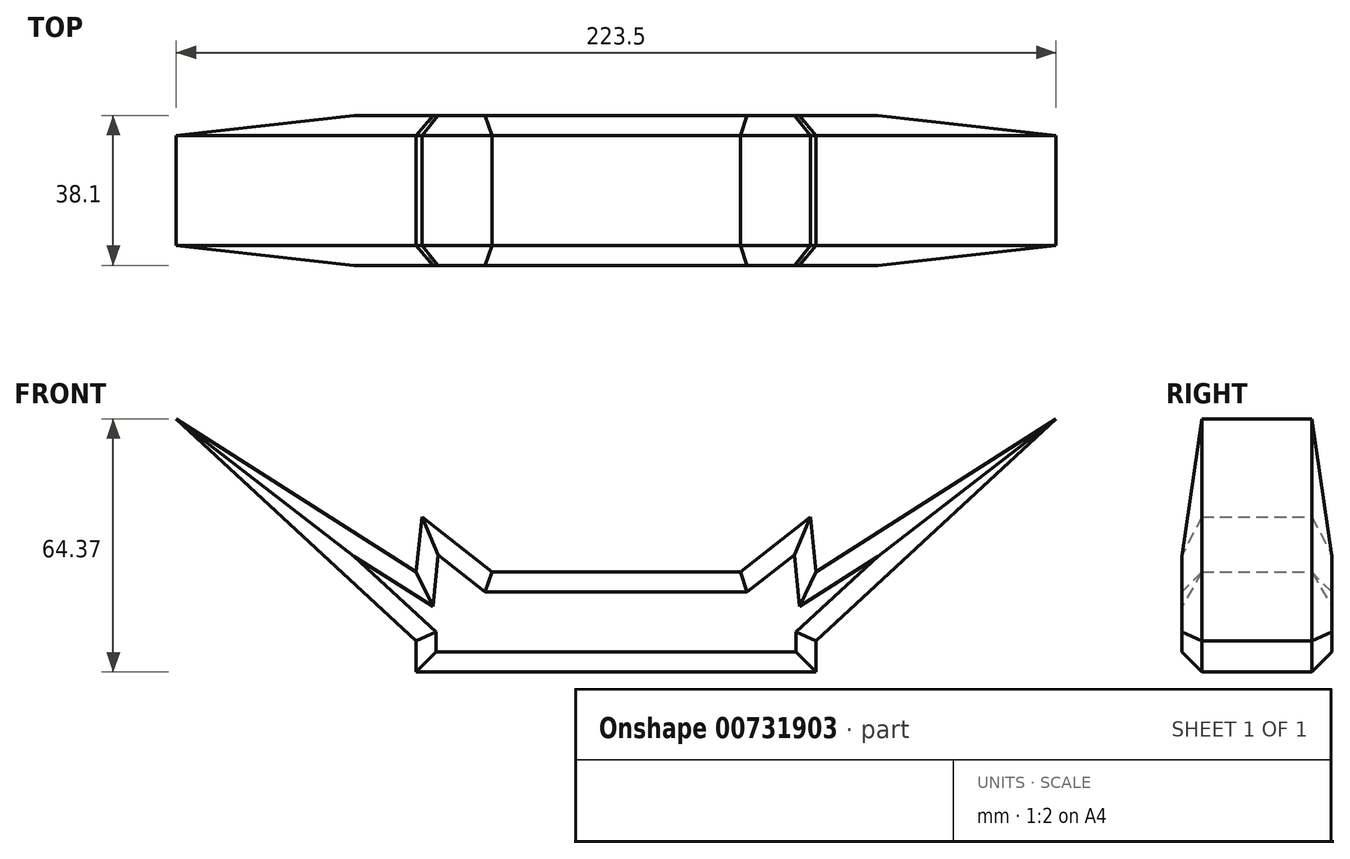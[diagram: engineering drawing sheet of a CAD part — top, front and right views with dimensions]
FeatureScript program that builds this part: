
annotation { "Feature Type Name" : "Feature", "Feature Type Description" : "" }
export const myFeature = defineFeature(function(context is Context, id is Id, definition is map)
    precondition{}
    {
        {
            var Q0;
            Q0=qCreatedBy(makeId("Front.planeOp"),FACE);
            var sketch = newSketch(context, id + "F0", { "sketchPlane" : qUnion([Q0])});
            skLineSegment(sketch, "E0", {"start": v(0, 12.7) * mm, "end": v(50.8, 12.7) * mm});
            skLineSegment(sketch, "E1", {"start": v(50.8, 12.7) * mm, "end": v(50.8, -12.7) * mm});
            skLineSegment(sketch, "E2", {"start": v(50.8, -12.7) * mm, "end": v(0, -12.7) * mm});
            skLineSegment(sketch, "E3.MirrorCS", {"start": v(0, 12.7) * mm, "end": v(-50.8, 12.7) * mm});
            skLineSegment(sketch, "E4.MirrorCS", {"start": v(-50.8, -12.7) * mm, "end": v(0, -12.7) * mm});
            skLineSegment(sketch, "E5.MirrorCS", {"start": v(-50.8, 12.7) * mm, "end": v(-50.8, -12.7) * mm});
            skLineSegment(sketch, "E6", {"start": v(-31.53, 12.7) * mm, "end": v(-49.37, 26.74) * mm});
            skLineSegment(sketch, "E7", {"start": v(-49.37, 26.74) * mm, "end": v(-50.8, 12.7) * mm});
            skLineSegment(sketch, "E8", {"start": v(-50.8, 12.7) * mm, "end": v(-111.75, 51.67) * mm});
            skLineSegment(sketch, "E9", {"start": v(-111.75, 51.67) * mm, "end": v(-50.8, -4.75) * mm});
            skLineSegment(sketch, "E10", {"start": v(0, 12.7) * mm, "end": v(0, -12.7) * mm});
            skLineSegment(sketch, "E11.MirrorCS", {"start": v(31.53, 12.7) * mm, "end": v(49.37, 26.74) * mm});
            skLineSegment(sketch, "E12.MirrorCS", {"start": v(49.37, 26.74) * mm, "end": v(50.8, 12.7) * mm});
            skLineSegment(sketch, "E13.MirrorCS", {"start": v(50.8, 12.7) * mm, "end": v(111.75, 51.67) * mm});
            skLineSegment(sketch, "E14.MirrorCS", {"start": v(111.75, 51.67) * mm, "end": v(50.8, -4.75) * mm});
            skSolve(sketch);
        }
        {
            var Q0;
            {var subQ0=sQuery(id+"F0.wireOp",EDGE,"E2");Q0=makeQuery(id+"F0.imprint","IMPRINT",FACE,{"disambiguationData":[TD([[makeQuery(id+"F0.imprint","IMPRINT",EDGE,{"derivedFrom":subQ0}),-1.0]])]});}
            var Q1;
            {var subQ2=sQuery(id+"F0.wireOp",EDGE,"E11.MirrorCS");Q1=makeQuery(id+"F0.imprint","IMPRINT",FACE,{"disambiguationData":[TD([[makeQuery(id+"F0.imprint","IMPRINT",EDGE,{"derivedFrom":subQ2}),-1.0]])]});}
            var Q2;
            {var subQ0=sQuery(id+"F0.wireOp",EDGE,"E13.MirrorCS");Q2=makeQuery(id+"F0.imprint","IMPRINT",FACE,{"disambiguationData":[TD([[makeQuery(id+"F0.imprint","IMPRINT",EDGE,{"derivedFrom":subQ0}),-1.0]])]});}
            var Q3;
            {var subQ2=sQuery(id+"F0.wireOp",EDGE,"E6");Q3=makeQuery(id+"F0.imprint","IMPRINT",FACE,{"disambiguationData":[TD([[makeQuery(id+"F0.imprint","IMPRINT",EDGE,{"derivedFrom":subQ2}),1.0]])]});}
            var Q4;
            {var subQ0=sQuery(id+"F0.wireOp",EDGE,"E8");Q4=makeQuery(id+"F0.imprint","IMPRINT",FACE,{"disambiguationData":[TD([[makeQuery(id+"F0.imprint","IMPRINT",EDGE,{"derivedFrom":subQ0}),1.0]])]});}
            var Q5;
            {var subQ4=sQuery(id+"F0.wireOp",EDGE,"E4.MirrorCS");Q5=makeQuery(id+"F0.imprint","IMPRINT",FACE,{"disambiguationData":[TD([[makeQuery(id+"F0.imprint","IMPRINT",EDGE,{"derivedFrom":subQ4}),1.0]])]});}
            extrude(context, id + "F1", {"entities" : qUnion([Q0, Q1, Q2, Q3, Q4, Q5]), "depth" : 19.05 * mm, "offsetDistance" : 25.4 * mm});
        }
        {
            var Q0;
            Q0=makeQuery(id+"F1.opExtrude","CAP_FACE",FACE,{"disambiguationData":[OSD([sQuery(id+"F0.wireOp",EDGE,"E0"),sQuery(id+"F0.wireOp",EDGE,"E1"),sQuery(id+"F0.wireOp",EDGE,"E2"),sQuery(id+"F0.wireOp",EDGE,"E3.MirrorCS"),sQuery(id+"F0.wireOp",EDGE,"E4.MirrorCS"),sQuery(id+"F0.wireOp",EDGE,"E5.MirrorCS"),sQuery(id+"F0.wireOp",EDGE,"E6"),sQuery(id+"F0.wireOp",EDGE,"E7"),sQuery(id+"F0.wireOp",EDGE,"E8"),sQuery(id+"F0.wireOp",EDGE,"E9"),sQuery(id+"F0.wireOp",EDGE,"E11.MirrorCS"),sQuery(id+"F0.wireOp",EDGE,"E12.MirrorCS"),sQuery(id+"F0.wireOp",EDGE,"E13.MirrorCS"),sQuery(id+"F0.wireOp",EDGE,"E14.MirrorCS")])],"isStart":true});
            extrude(context, id + "F2", {"entities" : qUnion([Q0]), "operationType" : NewBodyOperationType.ADD, "depth" : 19.05 * mm, "offsetDistance" : 25.4 * mm});
        }
        {
            var Q0;
            Q0=makeQuery(id+"F1.opExtrude","CAP_FACE",FACE,{"disambiguationData":[OSD([sQuery(id+"F0.wireOp",EDGE,"E0"),sQuery(id+"F0.wireOp",EDGE,"E1"),sQuery(id+"F0.wireOp",EDGE,"E2"),sQuery(id+"F0.wireOp",EDGE,"E3.MirrorCS"),sQuery(id+"F0.wireOp",EDGE,"E4.MirrorCS"),sQuery(id+"F0.wireOp",EDGE,"E5.MirrorCS"),sQuery(id+"F0.wireOp",EDGE,"E6"),sQuery(id+"F0.wireOp",EDGE,"E7"),sQuery(id+"F0.wireOp",EDGE,"E8"),sQuery(id+"F0.wireOp",EDGE,"E9"),sQuery(id+"F0.wireOp",EDGE,"E11.MirrorCS"),sQuery(id+"F0.wireOp",EDGE,"E12.MirrorCS"),sQuery(id+"F0.wireOp",EDGE,"E13.MirrorCS"),sQuery(id+"F0.wireOp",EDGE,"E14.MirrorCS")])],"isStart":false});
            var Q1;
            Q1=makeQuery(id+"F2.opExtrude","CAP_FACE",FACE,{"disambiguationData":[OSD([sQuery(id+"F0.wireOp",EDGE,"E0"),sQuery(id+"F0.wireOp",EDGE,"E1"),sQuery(id+"F0.wireOp",EDGE,"E2"),sQuery(id+"F0.wireOp",EDGE,"E3.MirrorCS"),sQuery(id+"F0.wireOp",EDGE,"E4.MirrorCS"),sQuery(id+"F0.wireOp",EDGE,"E5.MirrorCS"),sQuery(id+"F0.wireOp",EDGE,"E6"),sQuery(id+"F0.wireOp",EDGE,"E7"),sQuery(id+"F0.wireOp",EDGE,"E8"),sQuery(id+"F0.wireOp",EDGE,"E9"),sQuery(id+"F0.wireOp",EDGE,"E11.MirrorCS"),sQuery(id+"F0.wireOp",EDGE,"E12.MirrorCS"),sQuery(id+"F0.wireOp",EDGE,"E13.MirrorCS"),sQuery(id+"F0.wireOp",EDGE,"E14.MirrorCS")])],"isStart":false});
            chamfer(context, id + "F3", {"entities" : qUnion([Q0, Q1]), "width" : 5.08 * mm, "tangentPropagation" : true});
        }
    });
